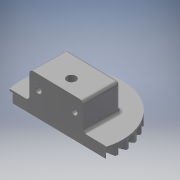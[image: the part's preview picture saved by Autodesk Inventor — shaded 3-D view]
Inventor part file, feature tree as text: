
AUTODESK INVENTOR PART (.ipt)
format: ipt  version: 2018 (Build 220112000, 112)  size: 406,528 bytes
history: native  units: mm (DEFAULTED — no unit token found)
features: extrude x8, other x8, sketch x8, projected_geometry x5, plane x3, reference x3, fillet x1
ambient origin geometry x8: Origin, YZ Plane, XZ Plane, XY Plane, X Axis, Y Axis, Z Axis, Center Point
bodies: Solid1 (feature_tree)
feature tree (36):
  extrude  "Extrusion1"  Depth=6.0mm TaperAngle=0.0deg
  plane  "Work Plane2"
  plane  "Work Plane8"
  plane  "Work Plane9"
  other  "Stirnzahnrad"
  extrude  "Extrusion6"  Depth=10.0mm TaperAngle=0.0deg
  extrude  "Extrusion7"  TaperAngle=0.0deg  [1 undecoded]
  extrude  "Extrusion8"  TaperAngle=0.0deg  [1 undecoded]
  extrude  "Extrusion9"  Depth=40.0mm
  extrude  "Extrusion10"  TaperAngle=0.0deg  [1 undecoded]
  extrude  "Extrusion11"  Depth=47.2mm
  extrude  "Extrusion12"  Depth=2.0mm
  fillet  "Rundung1"  Radius=20.0mm
  sketch  "Sketch1"  dims[d0=55.928942mm d1=6.0mm d2=0.0mm]
  sketch  "Sketch2"  dims[d3=53.333333mm d4=10.0mm d5=0.0mm]
  other  "Srf1"
  sketch  "Skizze9"  dims[d16=40.0mm d17=0.0mm]
  reference  "Referenz1"
  reference  "Referenz2"
  sketch  "Skizze10"  dims[d34=1.047198mm d39=0.0mm]
  projected_geometry  "Projizierte Kontur5"
  sketch  "Skizze11"  dims[d41=0.0mm d43=40.0mm]
  projected_geometry  "Projizierte Kontur6"
  reference  "Referenz3"
  sketch  "Skizze12"  dims[d46=40.0mm d47=0.0mm]
  projected_geometry  "Projizierte Kontur7"
  projected_geometry  "Projizierte Kontur8"
  sketch  "Skizze14"  dims[d48=0.0mm d83=47.2mm]
  projected_geometry  "Projizierte Kontur9"
  sketch  "Skizze15"  dims[d84=14.0mm d85=13.0mm d86=20.0mm d87=20.0mm d88=30.0mm d89=0.0mm d90=30.0mm d91=0.0mm d92=1.0mm d93=0.0mm d94=30.0mm d95=0.0mm d96=30.0mm d97=0.0mm d98=15.0mm d99=0.0mm d100=3.4mm d101=3.4mm d102=5.0mm d103=5.0mm d104=7.5mm d105=7.5mm d106=25.0mm d107=0.0mm d108=5.0mm d109=20.0mm d110=0.0mm d111=2.0mm]
  other  "Flankendurchmesser"
  other  "Stirnräder1.iam"
  other  "Stirnzahnrad2:1"
  other  "<userpath>\OneDrive\Development\Mohne\03_Konstruktion\StirnradUNDServo.iam"
  other  "StirnradUNDServo.iam"
  other  "L-Halterung Servo:1"
note: 3 required parameter values undecoded (feature->parameter linkage not recoverable at this tier; creation-order binding heuristic only, values carry confidence <= 0.55)
